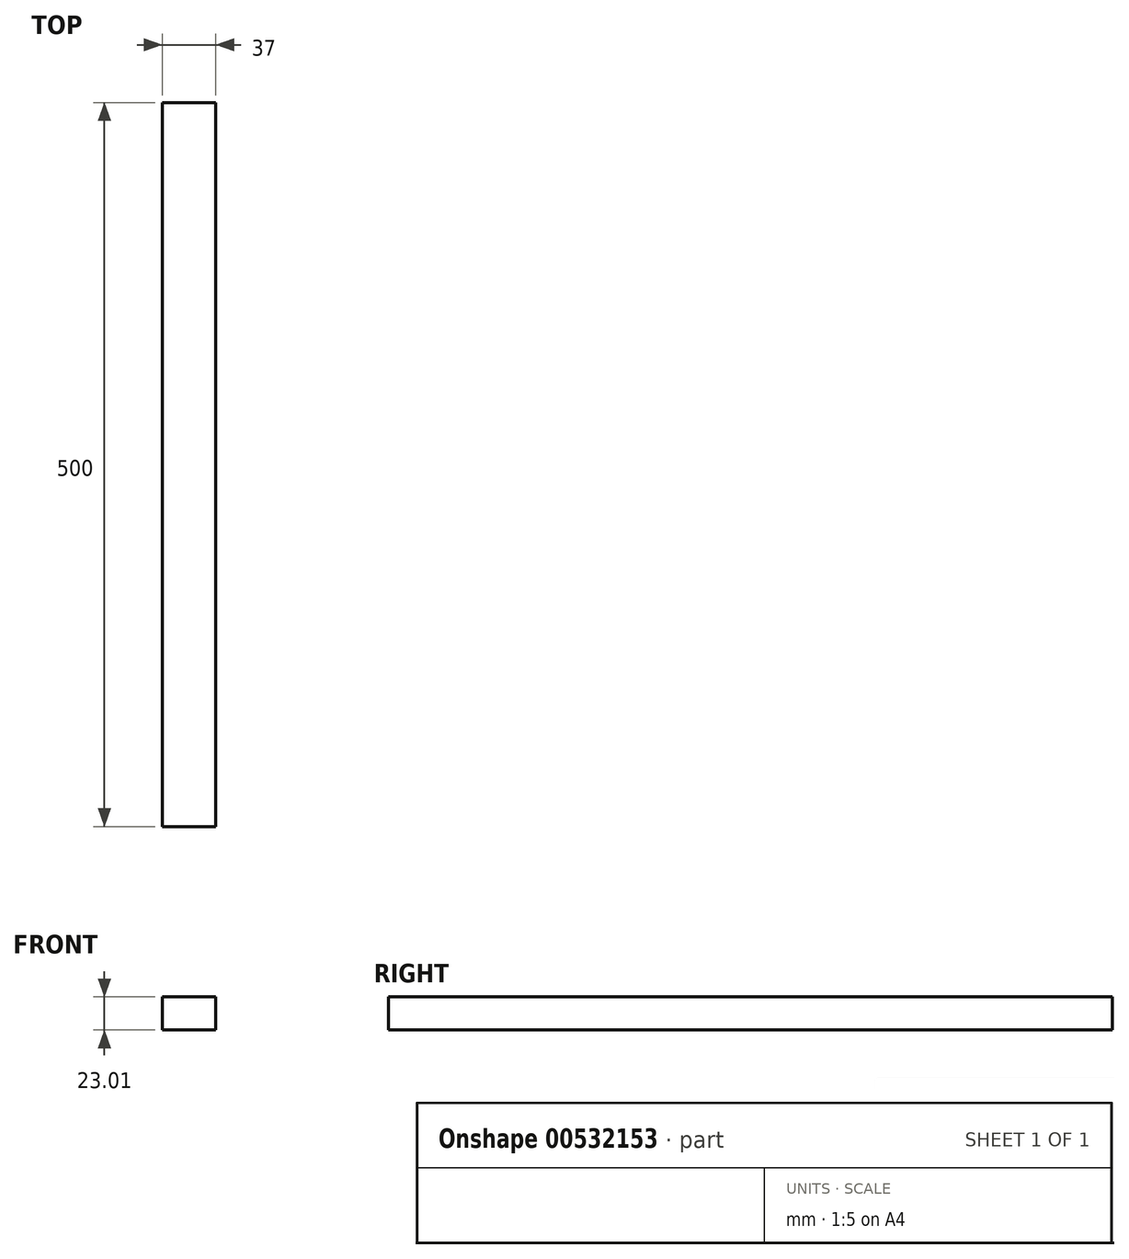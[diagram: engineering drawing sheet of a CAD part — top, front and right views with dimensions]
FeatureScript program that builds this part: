
annotation { "Feature Type Name" : "Feature", "Feature Type Description" : "" }
export const myFeature = defineFeature(function(context is Context, id is Id, definition is map)
    precondition{}
    {
        {
            var Q0;
            Q0=qCreatedBy(makeId("Front.planeOp"),FACE);
            var sketch = newSketch(context, id + "F0", { "sketchPlane" : qUnion([Q0])});
            skLineSegment(sketch, "E0.bottom", {"start": v(-37, 23) * mm, "end": v(0, 23) * mm});
            skLineSegment(sketch, "E0.top", {"start": v(-37, 0) * mm, "end": v(0, 0) * mm});
            skLineSegment(sketch, "E0.left", {"start": v(-37, 23) * mm, "end": v(-37, 0) * mm});
            skLineSegment(sketch, "E0.right", {"start": v(0, 23) * mm, "end": v(0, 0) * mm});
            skSolve(sketch);
        }
        {
            var Q0;
            Q0 = qSketchRegion(id + "F0", true);
            extrude(context, id + "F1", {"entities" : qUnion([Q0]), "depth" : 500 * mm, "offsetDistance" : 25 * mm});
        }
    });
